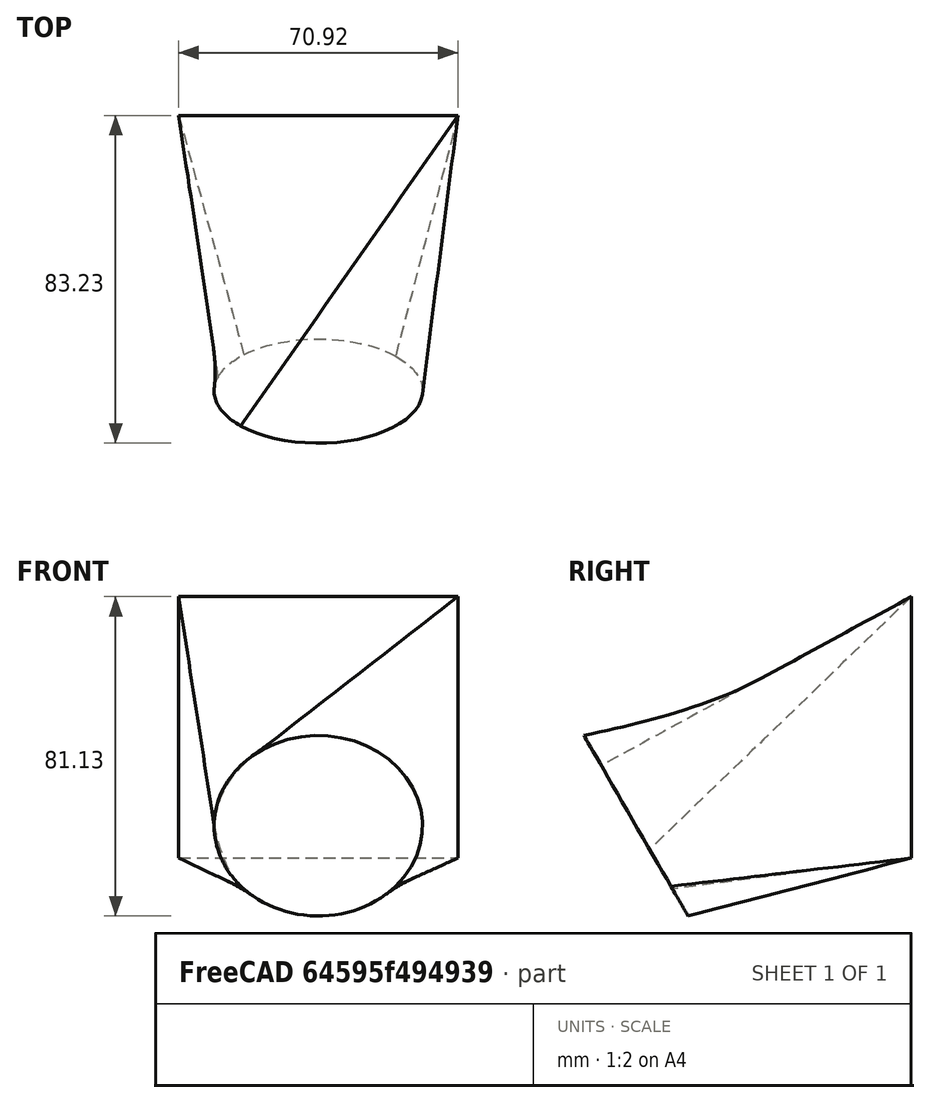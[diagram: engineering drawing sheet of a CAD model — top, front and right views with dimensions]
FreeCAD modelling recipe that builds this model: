
FCSTD DOCUMENT  (FreeCAD 0.20R29410 (Git))
Label: MangoJelly_Solutions_Tutorial_Ep11_3
License: All rights reserved
LicenseURL: http://en.wikipedia.org/wiki/All_rights_reserved
objects: Sketcher::SketchObject×2, Part::Loft×1
note: 3 computed .brp shape members not serialized (recipe doc carries the construction recipe); baked Part::Feature solids carry a one-line shape summary decoded from their .brp

FEATURE [Sketcher::SketchObject] Sketch
  FullyConstrained = false
  Placement = pos=(0,0,-25) rot=(1,0,0;2.0944rad)
  sketch-geometry (4):
    g0: ArcOfCircle CenterX=0 CenterY=0 CenterZ=0 NormalX=0 NormalY=0 NormalZ=1 AngleXU=0 Radius=26.464 StartAngle=5.54746 EndAngle=8.69395
    g1: ArcOfCircle CenterX=0 CenterY=0 CenterZ=0 NormalX=0 NormalY=0 NormalZ=1 AngleXU=0 Radius=26.464 StartAngle=2.41077 EndAngle=3.40841
    g2: ArcOfCircle CenterX=0 CenterY=0 CenterZ=0 NormalX=0 NormalY=0 NormalZ=1 AngleXU=0 Radius=26.464 StartAngle=3.40841 EndAngle=3.91658
    g3: ArcOfCircle CenterX=0 CenterY=0 CenterZ=0 NormalX=0 NormalY=0 NormalZ=1 AngleXU=0 Radius=26.464 StartAngle=3.91658 EndAngle=5.54746
  constraints (8):
    c: Coincident(g0,g-1)
    c: Coincident(g0,g1)
    c: Coincident(g0,g1)
    c: Coincident(g1,g2)
    c: Coincident(g1,g2)
    c: Coincident(g2,g3)
    c: Coincident(g2,g3)
    c: Coincident(g0,g3)
FEATURE [Sketcher::SketchObject] Sketch001
  FullyConstrained = false
  Placement = pos=(0,70,0) rot=(1,0,0;1.5708rad)
  sketch-geometry (5):
    g0: LineSegment StartX=-35.4603 StartY=33.2143 StartZ=0 EndX=-35.4603 EndY=-33.2143 EndZ=0
    g1: LineSegment StartX=-35.4603 StartY=-33.2143 StartZ=0 EndX=35.4603 EndY=-33.2143 EndZ=0
    g2: LineSegment StartX=35.4603 StartY=-33.2143 StartZ=0 EndX=35.4603 EndY=33.2143 EndZ=0
    g3: LineSegment StartX=35.4603 StartY=33.2143 StartZ=0 EndX=-35.4603 EndY=33.2143 EndZ=0
    g4: GeomPoint X=0 Y=0 Z=0
  constraints (10):
    c: Coincident(g0,g1)
    c: Coincident(g1,g2)
    c: Coincident(g2,g3)
    c: Coincident(g3,g0)
    c: Horizontal(g1)
    c: Horizontal(g3)
    c: Vertical(g0)
    c: Vertical(g2)
    c: Symmetric(g1,g0,g4)
    c: Coincident(g4,g-1)
FEATURE [Part::Loft] Loft
  Closed = false
  MaxDegree = 5
  Ruled = false
  Sections = -> [Sketch001,Sketch]
  Solid = true
